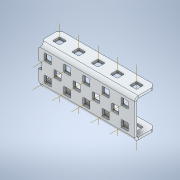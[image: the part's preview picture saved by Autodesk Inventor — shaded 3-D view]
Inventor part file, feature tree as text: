
AUTODESK INVENTOR PART (.ipt)
format: ipt  version: 2020 (Build 240168000, 168)  size: 1,175,552 bytes
history: native  units: in
note: dims shown in document units (in); Inventor stores cm internally (conversion verified against a paired STEP export)
features: other x28, plane x11, split x5, pattern_linear x4, sheet_metal_op x1
ambient origin geometry x8: Origin, YZ Plane, XZ Plane, XY Plane, X Axis, Y Axis, Z Axis, Center Point
bodies: Solid1 (feature_tree)
feature tree (49):
  other  "Work Axis1"
  pattern_linear  "Rectangular Pattern1"  Count1=5 Spacing1=0.5in
  other  "Work Axis72"
  pattern_linear  "Rectangular Pattern2"  Count1=5 Spacing1=0.5in
  pattern_linear  "Rectangular Pattern3"  Count1=5 Spacing1=0.5in
  other  "Work Axis141"
  pattern_linear  "Rectangular Pattern4"  Count1=4 Spacing1=0.5in
  plane  "Work Plane7"
  split  "Split1"
  plane  "Work Plane8"
  split  "Split2"
  plane  "Work Plane9"
  split  "Split3"
  plane  "Work Plane10"
  split  "Split4"
  plane  "Work Plane11"
  split  "Split5"
  plane  "Work Plane1"
  plane  "Work Plane2"
  other  "Work Point1"
  other  "Work Axis2"
  other  "Work Axis3"
  other  "Work Axis4"
  other  "Work Axis5"
  other  "Work Axis36"
  other  "Work Axis37"
  other  "Work Axis38"
  other  "Work Axis39"
  other  "Work Axis40"
  plane  "Work Plane3"
  plane  "Work Plane4"
  other  "Work Point2"
  other  "Work Axis71"
  other  "Work Point3"
  other  "Work Axis73"
  other  "Work Axis74"
  other  "Work Axis75"
  other  "Work Axis76"
  other  "Work Axis107"
  other  "Work Axis108"
  other  "Work Axis109"
  other  "Work Axis110"
  plane  "Work Plane5"
  plane  "Work Plane6"
  other  "Work Point4"
  other  "Work Axis142"
  other  "Work Axis143"
  other  "Work Axis144"
  sheet_metal_op  "Fold1"
